# Revit family: T100043
name_source: partatom
category: Furniture
revit_build: Autodesk Revit Architecture 2013 (Build: 20120221_2030(x64)
units: mm (PartAtom-declared; Revit-internal decimal feet)

## types (1)
- T100043
    Assembly Code = E2020200
    Back Coverage Material = OFS BRANDS IMPULSE Back Coverage Plastic
    Catalog = http://ofsbrands.com
    Chassis Material = OFS BRANDS IMPULSE Chassis Wood
    Depth = 72"
    Description = OFS BRANDS OFS IMPULSE G2 TYPICAL T100043
    Drawer Front Material = OFS BRANDS IMPULSE Drawer Front Wood
    Grommet  Material = OFS BRANDS IMPULSE Grommet Metal
    Height = 71 15/16"
    Lock Material = OFS BRANDS IMPULSE Lock Metal
    Manufacturer = OFS
    Model = T100043
    Pull Material = OFS BRANDS IMPULSE Pull Metal
    Top Core Material = OFS BRANDS IMPULSE Top Core Wood
    URL = http://www.ofsbrands.com
    Width = 66"

## geometry (parser evidence)
native form markers: Blend x2, Sweep x1
no freeform markers — native parametric forms only
